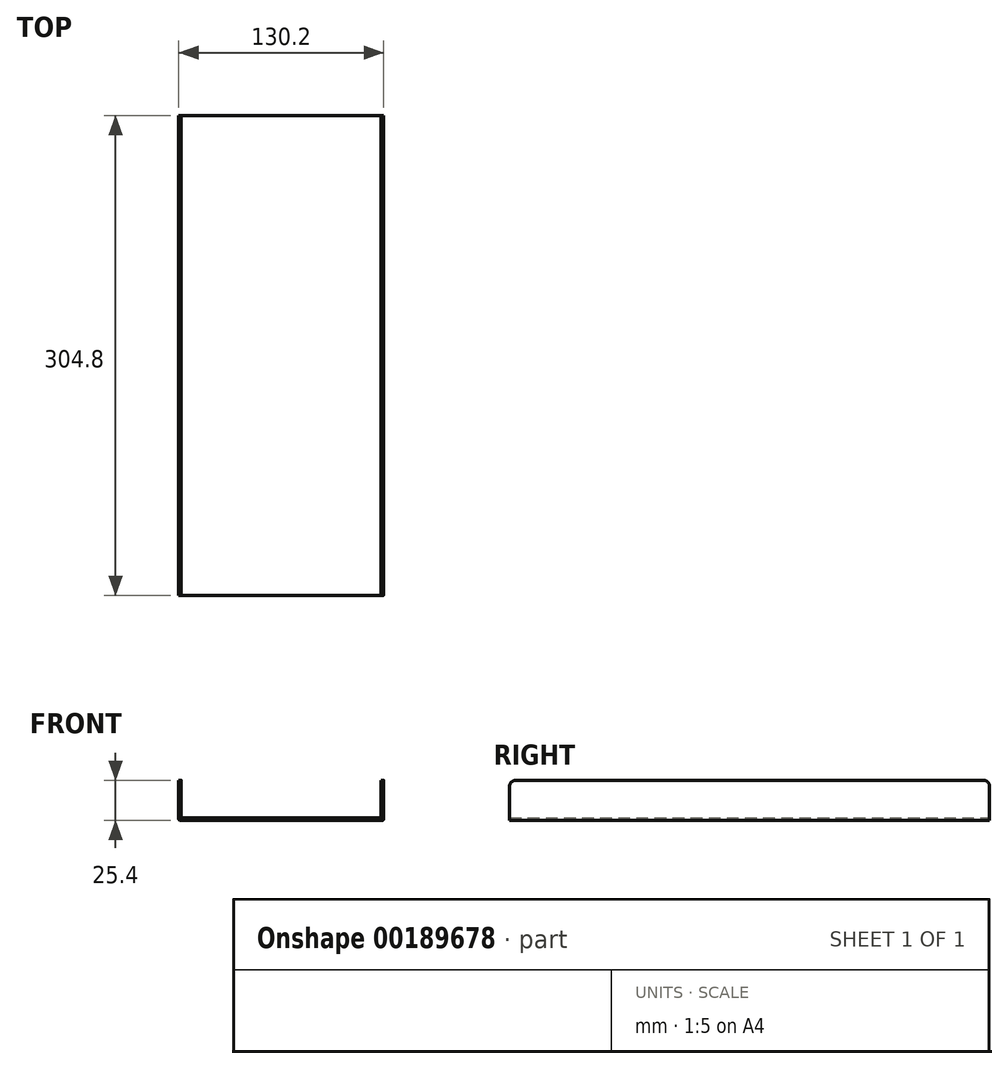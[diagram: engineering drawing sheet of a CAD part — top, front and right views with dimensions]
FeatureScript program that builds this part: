
annotation { "Feature Type Name" : "Feature", "Feature Type Description" : "" }
export const myFeature = defineFeature(function(context is Context, id is Id, definition is map)
    precondition{}
    {
        {
            assignVariable(context, id + "F0", {"name" : "thickness", "anyValue" : .63});
        }
        {
            assignVariable(context, id + "F1", {"name" : "inner_bend", "anyValue" : .25});
        }
        {
            var Q0;
            Q0=qCreatedBy(makeId("Front.planeOp"),FACE);
            var sketch = newSketch(context, id + "F2", { "sketchPlane" : qUnion([Q0])});
            skLineSegment(sketch, "E0", {"start": v(-65.1, 25.4) * mm, "end": v(-63.5, 25.4) * mm});
            skLineSegment(sketch, "E1", {"start": v(-63.5, 25.4) * mm, "end": v(-63.5, 1.6) * mm});
            skLineSegment(sketch, "E2", {"start": v(-63.5, 1.6) * mm, "end": v(63.5, 1.6) * mm});
            skLineSegment(sketch, "E3", {"start": v(63.5, 1.6) * mm, "end": v(63.5, 25.4) * mm});
            skLineSegment(sketch, "E4", {"start": v(63.5, 25.4) * mm, "end": v(65.1, 25.4) * mm});
            skLineSegment(sketch, "E5", {"start": v(65.1, 25.4) * mm, "end": v(65.1, 0) * mm});
            skLineSegment(sketch, "E6", {"start": v(65.1, 0) * mm, "end": v(-65.1, 0) * mm});
            skLineSegment(sketch, "E7", {"start": v(-65.1, 0) * mm, "end": v(-65.1, 25.4) * mm});
            skSolve(sketch);
        }
        {
            var Q0;
            Q0 = qSketchRegion(id + "F2", true);
            extrude(context, id + "F3", {"entities" : qUnion([Q0]), "depth" : 304.8 * mm});
        }
        {
            var Q0;
            Q0=makeQuery(id+"F3.opExtrude","SWEPT_EDGE",EDGE,{"disambiguationData":[OSD([sQuery(id+"F2.wireOp",EDGE,"E1"),sQuery(id+"F2.wireOp",EDGE,"E2")])]});
            var Q1;
            Q1=makeQuery(id+"F3.opExtrude","SWEPT_EDGE",EDGE,{"disambiguationData":[OSD([sQuery(id+"F2.wireOp",EDGE,"E2"),sQuery(id+"F2.wireOp",EDGE,"E3")])]});
            fillet(context, id + "F4", {"entities" : qUnion([Q0, Q1]), "radius" : (getVariable(context, 'inner_bend')) * mm, "tangentPropagation" : true, "allowEdgeOverflow" : false});
        }
        {
            var Q0;
            Q0=makeQuery(id+"F3.opExtrude","SWEPT_EDGE",EDGE,{"disambiguationData":[OSD([sQuery(id+"F2.wireOp",EDGE,"E5"),sQuery(id+"F2.wireOp",EDGE,"E6")])]});
            var Q1;
            Q1=makeQuery(id+"F3.opExtrude","SWEPT_EDGE",EDGE,{"disambiguationData":[OSD([sQuery(id+"F2.wireOp",EDGE,"E6"),sQuery(id+"F2.wireOp",EDGE,"E7")])]});
            fillet(context, id + "F5", {"entities" : qUnion([Q0, Q1]), "radius" : (getVariable(context, 'inner_bend') + getVariable(context, 'thickness')) * mm, "tangentPropagation" : true, "allowEdgeOverflow" : false});
        }
        {
            var Q0;
            Q0=makeQuery(id+"F3.opExtrude","CAP_EDGE",EDGE,{"disambiguationData":[OSD([sQuery(id+"F2.wireOp",EDGE,"E0")])],"isStart":false});
            var Q1;
            Q1=makeQuery(id+"F3.opExtrude","CAP_EDGE",EDGE,{"disambiguationData":[OSD([sQuery(id+"F2.wireOp",EDGE,"E4")])],"isStart":false});
            var Q2;
            Q2=makeQuery(id+"F3.opExtrude","CAP_EDGE",EDGE,{"disambiguationData":[OSD([sQuery(id+"F2.wireOp",EDGE,"E4")])],"isStart":true});
            var Q3;
            Q3=makeQuery(id+"F3.opExtrude","CAP_EDGE",EDGE,{"disambiguationData":[OSD([sQuery(id+"F2.wireOp",EDGE,"E0")])],"isStart":true});
            fillet(context, id + "F6", {"entities" : qUnion([Q0, Q1, Q2, Q3]), "radius" : 3.8 * mm, "tangentPropagation" : true, "allowEdgeOverflow" : false});
        }
    });
